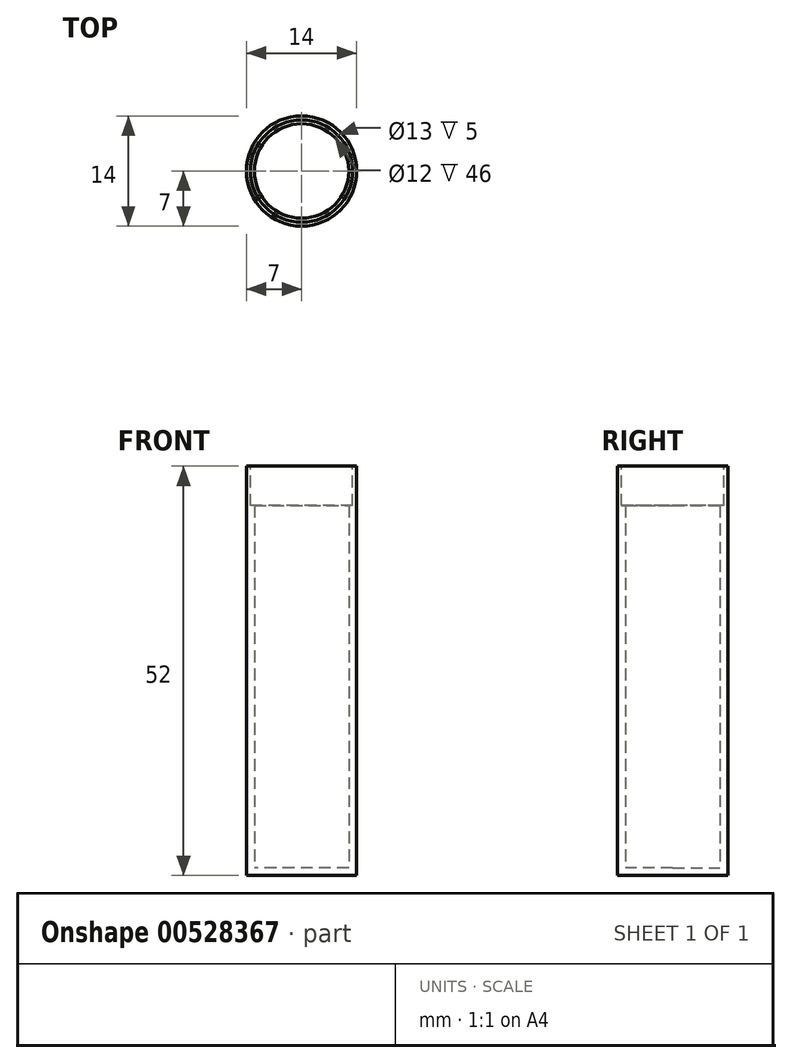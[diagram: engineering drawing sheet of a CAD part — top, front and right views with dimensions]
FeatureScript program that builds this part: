
annotation { "Feature Type Name" : "Feature", "Feature Type Description" : "" }
export const myFeature = defineFeature(function(context is Context, id is Id, definition is map)
    precondition{}
    {
        {
            var Q0;
            Q0=qCreatedBy(makeId("Front.planeOp"),FACE);
            var sketch = newSketch(context, id + "F0", { "sketchPlane" : qUnion([Q0])});
            skLineSegment(sketch, "E0", {"start": v(0, 0) * mm, "end": v(0, 27.24) * mm});
            skLineSegment(sketch, "E1", {"start": v(0, 27.24) * mm, "end": v(7, 27.24) * mm});
            skLineSegment(sketch, "E2", {"start": v(7, 27.24) * mm, "end": v(7, -24.76) * mm});
            skLineSegment(sketch, "E3", {"start": v(7, -24.76) * mm, "end": v(0, -24.76) * mm});
            skLineSegment(sketch, "E4", {"start": v(0, -24.76) * mm, "end": v(0, 0) * mm});
            skSolve(sketch);
        }
        {
            var Q0;
            Q0=makeQuery(id+"F0.imprint","IMPRINT",FACE,{"disambiguationData":[TD([[makeQuery(id+"F0.imprint","IMPRINT",EDGE,{"derivedFrom":sQuery(id+"F0.wireOp",EDGE,"E0")}),-1.0]])]});
            var Q1;
            Q1=sQuery(id+"F0.wireOp",EDGE,"E0");
            revolve(context, id + "F1", {"entities" : qUnion([Q0]), "axis" : qUnion([Q1]), "revolveType" : RevolveType.FULL});
        }
        {
            var Q0;
            Q0=makeQuery(id+"F1.opRevolve","SWEPT_FACE",FACE,{"disambiguationData":[OSD([sQuery(id+"F0.wireOp",EDGE,"E1")])]});
            shell(context, id + "F2", {"entities" : qUnion([Q0]), "thickness" : 1 * mm});
        }
        {
            var Q0;
            Q0=makeQuery(id+"F1.opRevolve","SWEPT_FACE",FACE,{"disambiguationData":[OSD([sQuery(id+"F0.wireOp",EDGE,"E1")])]});
            var sketch = newSketch(context, id + "F3", { "sketchPlane" : qUnion([Q0])});
            skCircle(sketch, "E5", {"center": v(0, 0) * mm, "radius": 6.5 * mm});
            skCircle(sketch, "E6", {"center": v(0, 0) * mm, "radius": 7.03 * mm});
            skSolve(sketch);
        }
        {
            var Q0;
            Q0=makeQuery(id+"F3.imprint","IMPRINT",FACE,{"disambiguationData":[TD([[makeQuery(id+"F3.imprint","IMPRINT",EDGE,{"derivedFrom":sQuery(id+"F3.wireOp",EDGE,"E5")}),1.0]])]});
            extrude(context, id + "F4", {"entities" : qUnion([Q0]), "operationType" : NewBodyOperationType.REMOVE, "oppositeDirection" : true, "depth" : 5 * mm, "offsetDistance" : 25.4 * mm});
        }
    });
